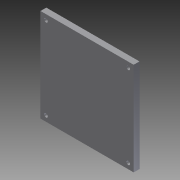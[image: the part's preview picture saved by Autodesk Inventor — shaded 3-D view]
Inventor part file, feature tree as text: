
AUTODESK INVENTOR PART (.ipt)
format: ipt  version: 2011 (Build 150239000, 239)  size: 124,928 bytes
history: native  units: in
note: dims shown in document units (in); Inventor stores cm internally (conversion verified against a paired STEP export)
features: extrude x7, sketch x7, fillet x1
ambient origin geometry x8: Origin, YZ Plane, XZ Plane, XY Plane, X Axis, Y Axis, Z Axis, Center Point
bodies: Solid1 (feature_tree)
feature tree (15):
  extrude  "Extrusion1"  Depth=4.0in
  extrude  "Extrusion2"  Depth=2.16in
  extrude  "Extrusion3"  Depth=1.7655in
  extrude  "Extrusion4"  Depth=0.029in TaperAngle=0.0deg
  extrude  "Extrusion5"  Depth=2.36in
  fillet  "Fillet1"  Radius=2.56in
  extrude  "Extrusion6"  Depth=0.125in
  extrude  "Extrusion7"  Depth=0.25in TaperAngle=0.0deg
  sketch  "Sketch1"  dims[d0=4.0in d1=4.0in]
  sketch  "Sketch2"  dims[d2=0.029in d3=0.0in d4=2.16in]
  sketch  "Sketch3"  dims[d5=0.029in d6=0.0in d7=1.7655in]
  sketch  "Sketch4"  dims[d8=0.156in d9=0.029in d10=0.0in]
  sketch  "Sketch5"  dims[d11=0.029in d12=0.0in d13=2.36in d14=2.56in]
  sketch  "Sketch6"  dims[d15=0.262in d16=0.0in d17=0.125in]
  sketch  "Sketch7"  dims[d18=0.25in d19=0.0in d20=0.25in d21=0.0in]
